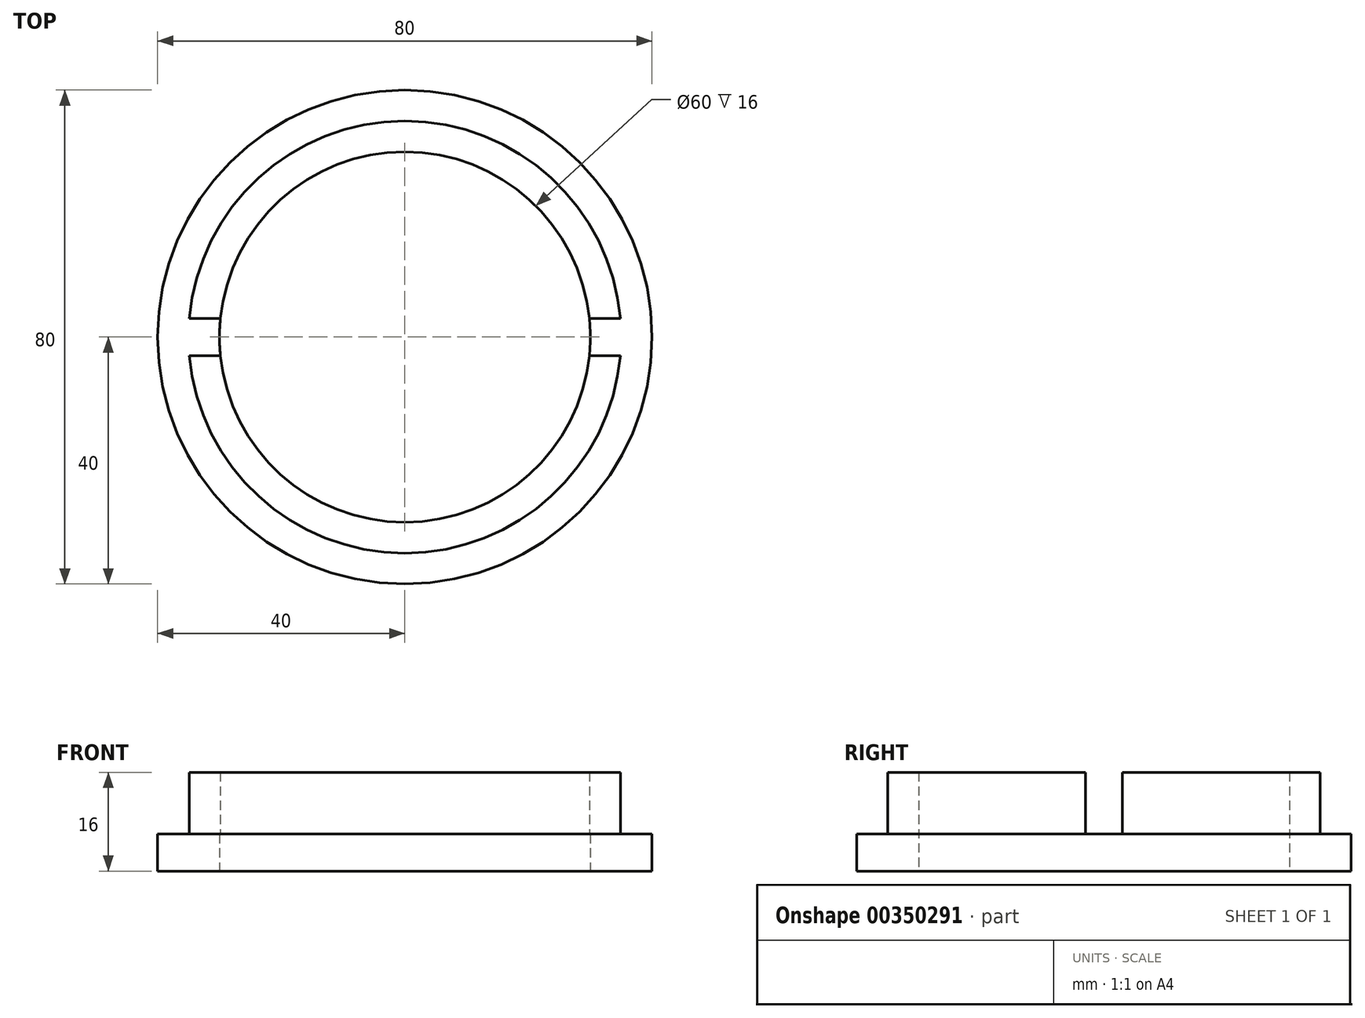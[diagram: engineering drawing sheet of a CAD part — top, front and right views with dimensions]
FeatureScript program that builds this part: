
annotation { "Feature Type Name" : "Feature", "Feature Type Description" : "" }
export const myFeature = defineFeature(function(context is Context, id is Id, definition is map)
    precondition{}
    {
        {
            var Q0;
            Q0=qCreatedBy(makeId("Front.planeOp"),FACE);
            var sketch = newSketch(context, id + "F0", { "sketchPlane" : qUnion([Q0])});
            skLineSegment(sketch, "E0", {"start": v(-30, 0) * mm, "end": v(-30, 16) * mm});
            skLineSegment(sketch, "E1", {"start": v(-30, 16) * mm, "end": v(-35, 16) * mm});
            skLineSegment(sketch, "E2", {"start": v(-35, 16) * mm, "end": v(-35, 6) * mm});
            skLineSegment(sketch, "E3", {"start": v(-35, 6) * mm, "end": v(-40, 6) * mm});
            skLineSegment(sketch, "E4", {"start": v(-40, 6) * mm, "end": v(-40, 0) * mm});
            skLineSegment(sketch, "E5", {"start": v(-40, 0) * mm, "end": v(-30, 0) * mm});
            skLineSegment(sketch, "E6", {"start": v(0, 0) * mm, "end": v(0, 30.65) * mm, "construction": true});
            skSolve(sketch);
        }
        {
            var Q0;
            Q0=makeQuery(id+"F0.imprint","IMPRINT",FACE,{"disambiguationData":[TD([[makeQuery(id+"F0.imprint","IMPRINT",EDGE,{"derivedFrom":sQuery(id+"F0.wireOp",EDGE,"E0")}),1.0]])]});
            var Q1;
            Q1=sQuery(id+"F0.wireOp",EDGE,"E6");
            revolve(context, id + "F1", {"entities" : qUnion([Q0]), "axis" : qUnion([Q1]), "revolveType" : RevolveType.FULL});
        }
        {
            var Q0;
            Q0=qCreatedBy(makeId("Right.planeOp"),FACE);
            var sketch = newSketch(context, id + "F2", { "sketchPlane" : qUnion([Q0])});
            skLineSegment(sketch, "E7.bottom", {"start": v(-3, 16) * mm, "end": v(3, 16) * mm});
            skLineSegment(sketch, "E7.top", {"start": v(-3, 6) * mm, "end": v(3, 6) * mm});
            skLineSegment(sketch, "E7.left", {"start": v(-3, 16) * mm, "end": v(-3, 6) * mm});
            skLineSegment(sketch, "E7.right", {"start": v(3, 16) * mm, "end": v(3, 6) * mm});
            skSolve(sketch);
        }
        {
            var Q0;
            Q0=makeQuery(id+"F2.imprint","IMPRINT",FACE,{"disambiguationData":[TD([[makeQuery(id+"F2.imprint","IMPRINT",EDGE,{"derivedFrom":sQuery(id+"F2.wireOp",EDGE,"E7.bottom")}),-1.0]])]});
            extrude(context, id + "F3", {"entities" : qUnion([Q0]), "operationType" : NewBodyOperationType.REMOVE, "endBound" : BoundingType.SYMMETRIC, "depth" : 100 * mm});
        }
    });
